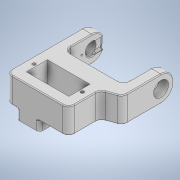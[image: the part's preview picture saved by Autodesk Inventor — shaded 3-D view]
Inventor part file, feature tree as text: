
AUTODESK INVENTOR PART (.ipt)
format: ipt  version: 2020.3 (Build 243373000, 373)  size: 446,976 bytes
history: native  units: mm
features: sketch x5, other x3
ambient origin geometry x8: Origin, YZ Plane, XZ Plane, XY Plane, X Axis, Y Axis, Z Axis, Center Point
bodies: Solid1 (feature_tree)
feature tree (8):
  other  "LegStart_v1.ipt"
  other  "Solid1::LegStart_v1.ipt"
  other  "TaggingFeature1"
  sketch  "Sketch1"  dims[d0=10.0mm]
  sketch  "Sketch2"
  sketch  "Sketch3"
  sketch  "Sketch8"
  sketch  "Sketch9"
